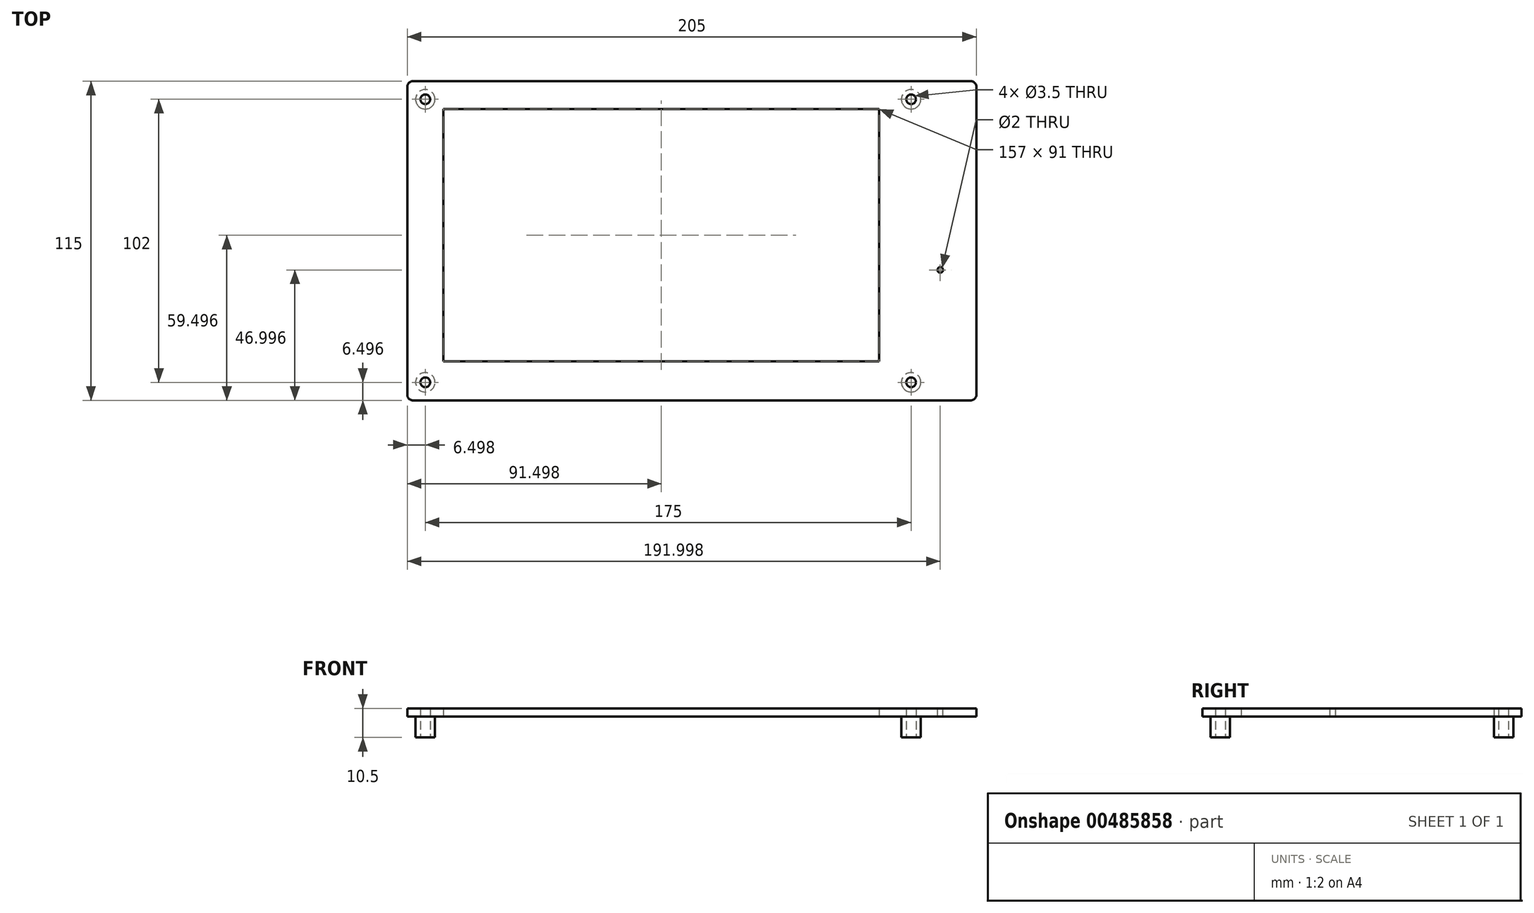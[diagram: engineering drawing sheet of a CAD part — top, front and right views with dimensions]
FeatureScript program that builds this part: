
annotation { "Feature Type Name" : "Feature", "Feature Type Description" : "" }
export const myFeature = defineFeature(function(context is Context, id is Id, definition is map)
    precondition{}
    {
        {
            var Q0;
            Q0=qCreatedBy(makeId("Top.planeOp"),FACE);
            var sketch = newSketch(context, id + "F0", { "sketchPlane" : qUnion([Q0])});
            skLineSegment(sketch, "E0.bottom", {"start": v(-118.8, 63.24) * mm, "end": v(86.2, 63.24) * mm});
            skLineSegment(sketch, "E0.top", {"start": v(-118.8, -51.76) * mm, "end": v(86.2, -51.76) * mm});
            skLineSegment(sketch, "E0.left", {"start": v(-118.8, 63.24) * mm, "end": v(-118.8, -51.76) * mm});
            skLineSegment(sketch, "E0.right", {"start": v(86.2, 63.24) * mm, "end": v(86.2, -51.76) * mm});
            skLineSegment(sketch, "E1", {"start": v(-105.8, 53.24) * mm, "end": v(-105.8, -37.76) * mm});
            skLineSegment(sketch, "E2", {"start": v(-105.8, -37.76) * mm, "end": v(51.2, -37.76) * mm});
            skLineSegment(sketch, "E3", {"start": v(51.2, -37.76) * mm, "end": v(51.2, 53.24) * mm});
            skLineSegment(sketch, "E4", {"start": v(-105.8, 53.24) * mm, "end": v(51.2, 53.24) * mm});
            skCircle(sketch, "E5", {"center": v(-112.3, 56.74) * mm, "radius": 1.75 * mm});
            skCircle(sketch, "E6", {"center": v(-112.3, -45.26) * mm, "radius": 1.75 * mm});
            skCircle(sketch, "E7", {"center": v(62.7, -45.26) * mm, "radius": 1.75 * mm});
            skCircle(sketch, "E8", {"center": v(62.7, 56.74) * mm, "radius": 1.75 * mm});
            skSolve(sketch);
        }
        {
            var Q0;
            Q0=makeQuery(id+"F0.imprint","IMPRINT",FACE,{"disambiguationData":[TD([[makeQuery(id+"F0.imprint","IMPRINT",EDGE,{"derivedFrom":sQuery(id+"F0.wireOp",EDGE,"E0.bottom")}),-1.0]])]});
            extrude(context, id + "F1", {"entities" : qUnion([Q0]), "depth" : 3 * mm});
        }
        {
            var Q0;
            Q0=makeQuery(id+"F1.opExtrude","SWEPT_EDGE",EDGE,{"disambiguationData":[OSD([sQuery(id+"F0.wireOp",EDGE,"E0.top"),sQuery(id+"F0.wireOp",EDGE,"E0.left")])]});
            var Q1;
            Q1=makeQuery(id+"F1.opExtrude","SWEPT_EDGE",EDGE,{"disambiguationData":[OSD([sQuery(id+"F0.wireOp",EDGE,"E0.bottom"),sQuery(id+"F0.wireOp",EDGE,"E0.left")])]});
            var Q2;
            Q2=makeQuery(id+"F1.opExtrude","SWEPT_EDGE",EDGE,{"disambiguationData":[OSD([sQuery(id+"F0.wireOp",EDGE,"E0.top"),sQuery(id+"F0.wireOp",EDGE,"E0.right")])]});
            var Q3;
            Q3=makeQuery(id+"F1.opExtrude","SWEPT_EDGE",EDGE,{"disambiguationData":[OSD([sQuery(id+"F0.wireOp",EDGE,"E0.bottom"),sQuery(id+"F0.wireOp",EDGE,"E0.right")])]});
            fillet(context, id + "F2", {"entities" : qUnion([Q0, Q1, Q2, Q3]), "radius" : 2 * mm, "tangentPropagation" : true, "allowEdgeOverflow" : false});
        }
        {
            var Q0;
            Q0 = qSketchRegion(id + "F0", true);
            extrude(context, id + "F3", {"entities" : qUnion([Q0]), "operationType" : NewBodyOperationType.REMOVE, "oppositeDirection" : true, "depth" : 25 * mm});
        }
        {
            var Q0;
            Q0=makeQuery(id+"F1.opExtrude","CAP_FACE",FACE,{"disambiguationData":[OSD([sQuery(id+"F0.wireOp",EDGE,"E0.bottom"),sQuery(id+"F0.wireOp",EDGE,"E0.top"),sQuery(id+"F0.wireOp",EDGE,"E0.left"),sQuery(id+"F0.wireOp",EDGE,"E0.right"),sQuery(id+"F0.wireOp",EDGE,"E1"),sQuery(id+"F0.wireOp",EDGE,"E2"),sQuery(id+"F0.wireOp",EDGE,"E3"),sQuery(id+"F0.wireOp",EDGE,"E4"),sQuery(id+"F0.wireOp",EDGE,"E5"),sQuery(id+"F0.wireOp",EDGE,"E6"),sQuery(id+"F0.wireOp",EDGE,"E7"),sQuery(id+"F0.wireOp",EDGE,"E8")])],"isStart":false});
            var sketch = newSketch(context, id + "F4", { "sketchPlane" : qUnion([Q0])});
            skPoint(sketch, "E9", {"position": v(73.2, -4.76) * mm});
            skCircle(sketch, "E10", {"center": v(73.2, -4.76) * mm, "radius": 1 * mm});
            skSolve(sketch);
        }
        {
            var Q0;
            Q0 = qSketchRegion(id + "F4", true);
            extrude(context, id + "F5", {"entities" : qUnion([Q0]), "operationType" : NewBodyOperationType.REMOVE, "oppositeDirection" : true, "depth" : 25 * mm});
        }
        {
            var Q0;
            Q0=makeQuery(id+"F1.opExtrude","CAP_FACE",FACE,{"disambiguationData":[OSD([sQuery(id+"F0.wireOp",EDGE,"E0.bottom"),sQuery(id+"F0.wireOp",EDGE,"E0.top"),sQuery(id+"F0.wireOp",EDGE,"E0.left"),sQuery(id+"F0.wireOp",EDGE,"E0.right"),sQuery(id+"F0.wireOp",EDGE,"E1"),sQuery(id+"F0.wireOp",EDGE,"E2"),sQuery(id+"F0.wireOp",EDGE,"E3"),sQuery(id+"F0.wireOp",EDGE,"E4"),sQuery(id+"F0.wireOp",EDGE,"E5"),sQuery(id+"F0.wireOp",EDGE,"E6"),sQuery(id+"F0.wireOp",EDGE,"E7"),sQuery(id+"F0.wireOp",EDGE,"E8")])],"isStart":true});
            var sketch = newSketch(context, id + "F6", { "sketchPlane" : qUnion([Q0])});
            skCircle(sketch, "E11", {"center": v(-112.3, 45.26) * mm, "radius": 3.5 * mm});
            skCircle(sketch, "E12", {"center": v(-112.3, -56.74) * mm, "radius": 3.5 * mm});
            skCircle(sketch, "E13", {"center": v(62.7, 45.26) * mm, "radius": 3.5 * mm});
            skCircle(sketch, "E14", {"center": v(62.7, -56.74) * mm, "radius": 3.5 * mm});
            skSolve(sketch);
        }
        {
            var Q0;
            Q0 = qSketchRegion(id + "F6", true);
            extrude(context, id + "F7", {"entities" : qUnion([Q0]), "operationType" : NewBodyOperationType.ADD, "depth" : 7.5 * mm});
        }
        {
            var Q0;
            Q0=makeQuery(id+"F7.opExtrude","CAP_FACE",FACE,{"disambiguationData":[OSD([sQuery(id+"F6.wireOp",EDGE,"E11")])],"isStart":false});
            var sketch = newSketch(context, id + "F8", { "sketchPlane" : qUnion([Q0])});
            skCircle(sketch, "E15", {"center": v(-112.3, 45.26) * mm, "radius": 1.75 * mm});
            skSolve(sketch);
        }
        {
            var Q0;
            Q0 = qSketchRegion(id + "F8", true);
            extrude(context, id + "F9", {"entities" : qUnion([Q0]), "operationType" : NewBodyOperationType.REMOVE, "oppositeDirection" : true, "depth" : 25 * mm});
        }
        {
            var Q0;
            Q0=makeQuery(id+"F7.opExtrude","CAP_FACE",FACE,{"disambiguationData":[OSD([sQuery(id+"F6.wireOp",EDGE,"E12")])],"isStart":false});
            var sketch = newSketch(context, id + "F10", { "sketchPlane" : qUnion([Q0])});
            skCircle(sketch, "E16", {"center": v(-112.3, -56.74) * mm, "radius": 1.75 * mm});
            skSolve(sketch);
        }
        {
            var Q0;
            Q0 = qSketchRegion(id + "F10", true);
            extrude(context, id + "F11", {"entities" : qUnion([Q0]), "operationType" : NewBodyOperationType.REMOVE, "oppositeDirection" : true, "depth" : 25 * mm});
        }
        {
            var Q0;
            Q0=makeQuery(id+"F7.opExtrude","CAP_FACE",FACE,{"disambiguationData":[OSD([sQuery(id+"F6.wireOp",EDGE,"E14")])],"isStart":false});
            var sketch = newSketch(context, id + "F12", { "sketchPlane" : qUnion([Q0])});
            skCircle(sketch, "E17", {"center": v(62.7, -56.74) * mm, "radius": 1.75 * mm});
            skSolve(sketch);
        }
        {
            var Q0;
            Q0 = qSketchRegion(id + "F12", true);
            extrude(context, id + "F13", {"entities" : qUnion([Q0]), "operationType" : NewBodyOperationType.REMOVE, "oppositeDirection" : true, "depth" : 25 * mm});
        }
        {
            var Q0;
            Q0=makeQuery(id+"F7.opExtrude","CAP_FACE",FACE,{"disambiguationData":[OSD([sQuery(id+"F6.wireOp",EDGE,"E13")])],"isStart":false});
            var sketch = newSketch(context, id + "F14", { "sketchPlane" : qUnion([Q0])});
            skCircle(sketch, "E18", {"center": v(62.7, 45.26) * mm, "radius": 1.75 * mm});
            skSolve(sketch);
        }
        {
            var Q0;
            Q0 = qSketchRegion(id + "F14", true);
            extrude(context, id + "F15", {"entities" : qUnion([Q0]), "operationType" : NewBodyOperationType.REMOVE, "oppositeDirection" : true, "depth" : 25 * mm});
        }
    });
